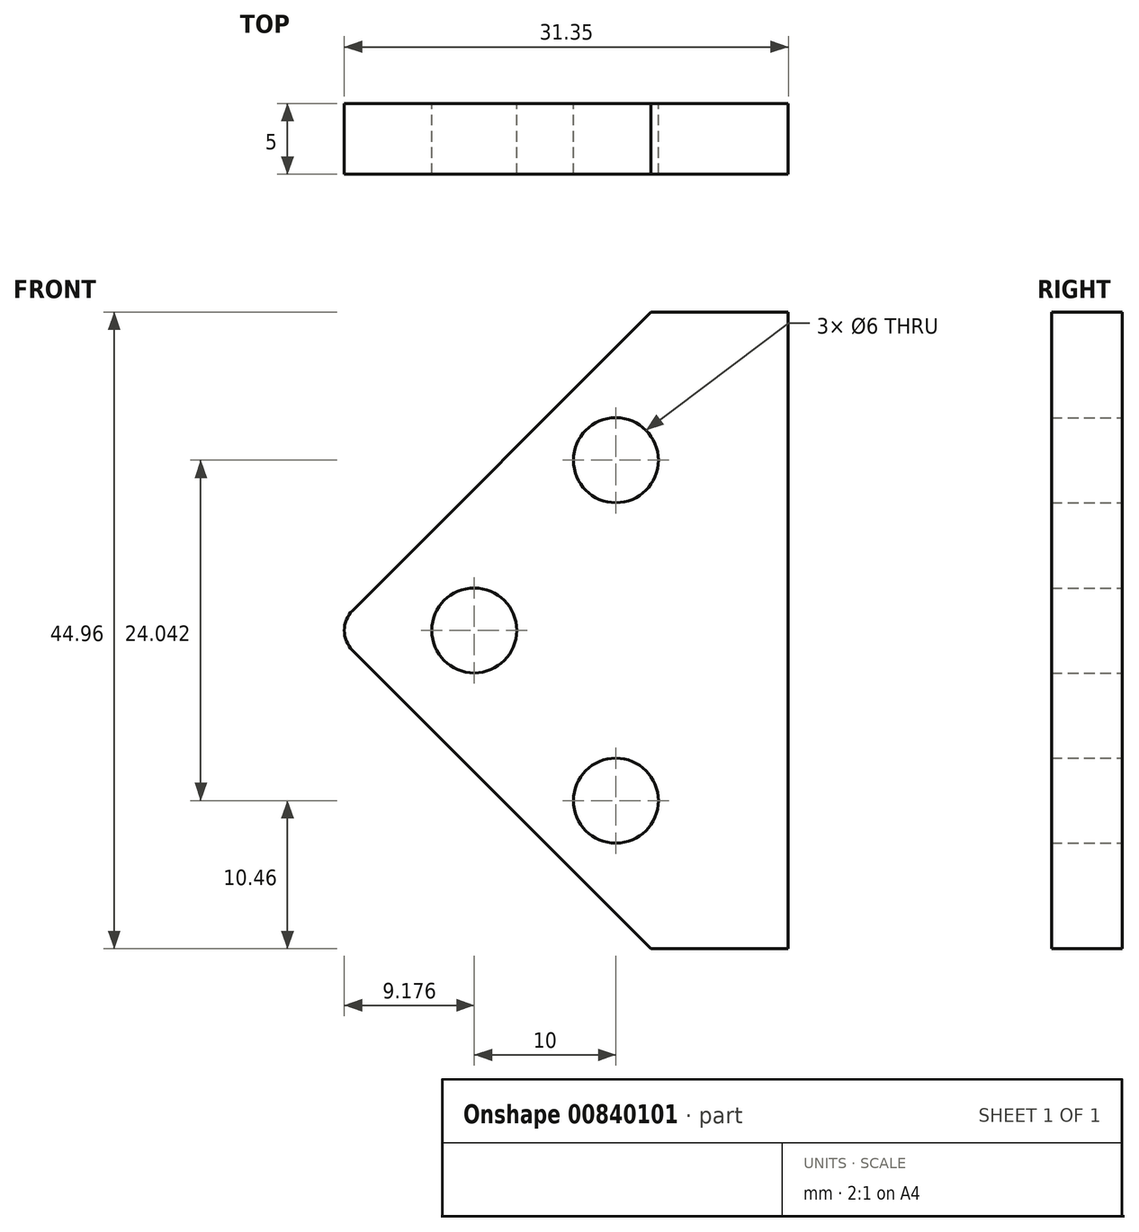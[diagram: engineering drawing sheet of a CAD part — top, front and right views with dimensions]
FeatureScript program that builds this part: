
annotation { "Feature Type Name" : "Feature", "Feature Type Description" : "" }
export const myFeature = defineFeature(function(context is Context, id is Id, definition is map)
    precondition{}
    {
        {
            var Q0;
            Q0=qCreatedBy(makeId("Front.planeOp"),FACE);
            var sketch = newSketch(context, id + "F0", { "sketchPlane" : qUnion([Q0])});
            skLineSegment(sketch, "E0", {"start": v(-9.07, -9.35) * mm, "end": v(-18.76, -9.35) * mm});
            skPoint(sketch, "E1", {"position": v(-31.24, 13.13) * mm});
            skCircle(sketch, "E2", {"center": v(-31.24, 13.13) * mm, "radius": 3 * mm});
            skPoint(sketch, "E3", {"position": v(-21.24, 25.15) * mm});
            skPoint(sketch, "E4", {"position": v(-21.24, 1.1) * mm});
            skCircle(sketch, "E5", {"center": v(-21.24, 25.15) * mm, "radius": 3 * mm});
            skCircle(sketch, "E6", {"center": v(-21.24, 1.1) * mm, "radius": 3 * mm});
            skLineSegment(sketch, "E7", {"start": v(-9.07, 35.6) * mm, "end": v(-9.07, -9.35) * mm});
            skLineSegment(sketch, "E8", {"start": v(-39.83, 11.72) * mm, "end": v(-18.76, -9.35) * mm});
            skPoint(sketch, "E9", {"position": v(-38.42, 13.13) * mm});
            skArc(sketch, "E10", {"start": v(-39.83, 14.54) * mm, "mid": v(-40.42, 13.13) * mm, "end": v(-39.83, 11.72) * mm});
            skLineSegment(sketch, "E11", {"start": v(-18.76, 35.6) * mm, "end": v(-9.07, 35.6) * mm});
            skLineSegment(sketch, "E12", {"start": v(-39.83, 14.54) * mm, "end": v(-18.76, 35.6) * mm});
            skSolve(sketch);
        }
        {
            var Q0;
            Q0=qSketchRegion(id+"F0",true);
            extrude(context, id + "F1", {"entities" : qUnion([Q0]), "depth" : 5 * mm, "offsetDistance" : 25 * mm});
        }
    });
